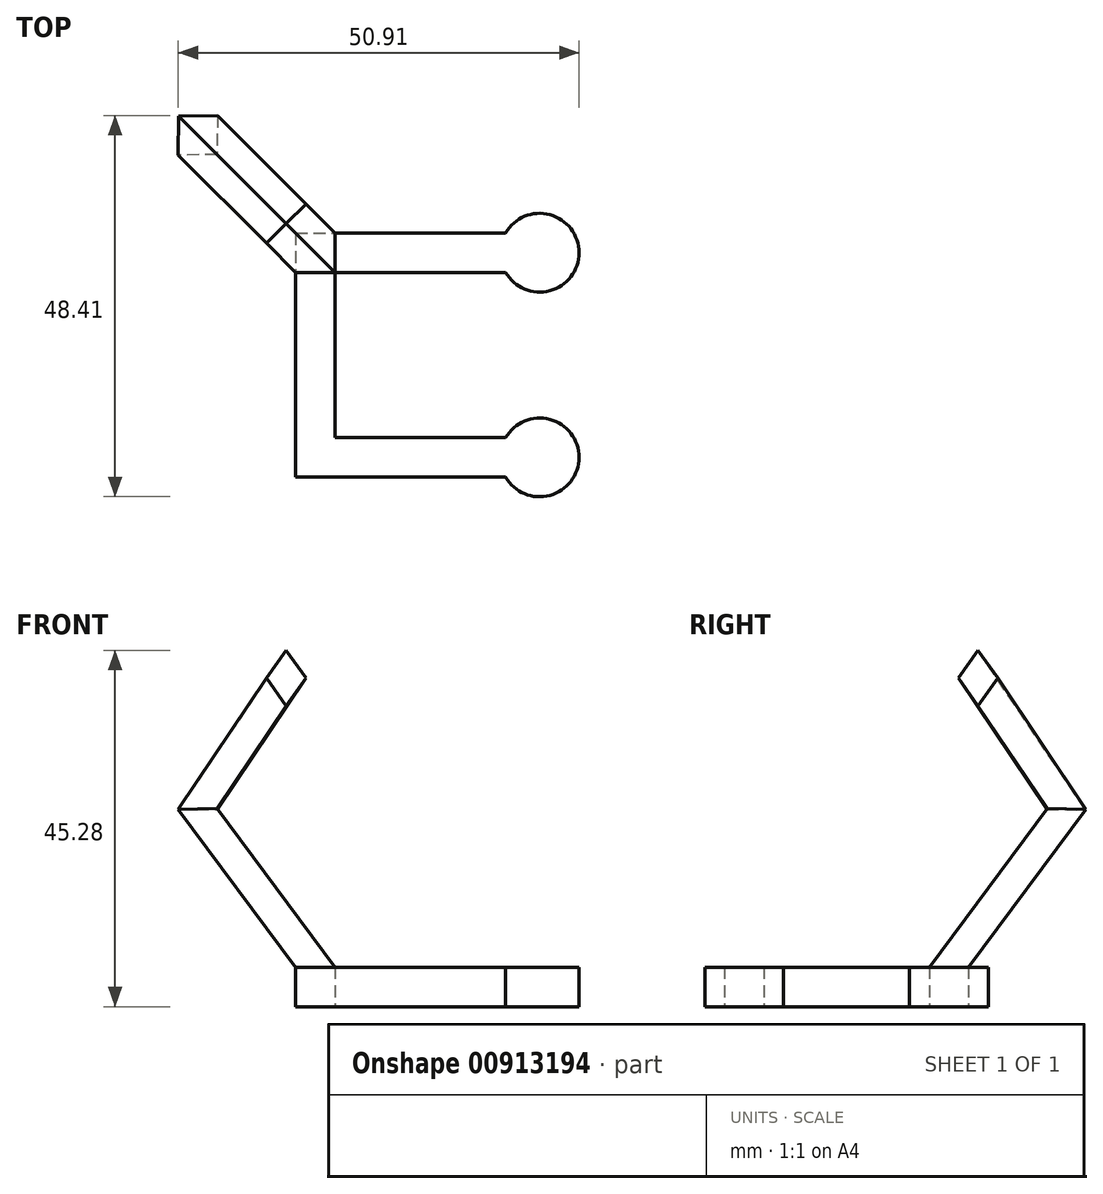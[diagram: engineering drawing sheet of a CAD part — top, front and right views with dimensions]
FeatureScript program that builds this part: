
annotation { "Feature Type Name" : "Feature", "Feature Type Description" : "" }
export const myFeature = defineFeature(function(context is Context, id is Id, definition is map)
    precondition{}
    {
        {
            assignVariable(context, id + "F0", {"name" : "HangerThickness", "anyValue" : 5});
        }
        {
            var Q0;
            Q0=qCreatedBy(makeId("Top.planeOp"),FACE);
            var sketch = newSketch(context, id + "F1", { "sketchPlane" : qUnion([Q0])});
            skLineSegment(sketch, "E0.bottom", {"start": v(10.5, 10.5) * mm, "end": v(-10.5, 10.5) * mm});
            skLineSegment(sketch, "E0.top", {"start": v(10.5, -10.5) * mm, "end": v(-10.5, -10.5) * mm});
            skLineSegment(sketch, "E0.left", {"start": v(10.5, 10.5) * mm, "end": v(10.5, -10.5) * mm});
            skLineSegment(sketch, "E0.right", {"start": v(-10.5, 10.5) * mm, "end": v(-10.5, -10.5) * mm});
            skPoint(sketch, "E0.middle", {"position": v(0, 0) * mm});
            skLineSegment(sketch, "E1.bottom", {"start": v(-15.5, 15.5) * mm, "end": v(15.5, 15.5) * mm});
            skLineSegment(sketch, "E1.top", {"start": v(-15.5, 10.5) * mm, "end": v(15.5, 10.5) * mm});
            skLineSegment(sketch, "E1.left", {"start": v(-15.5, 15.5) * mm, "end": v(-15.5, 10.5) * mm});
            skLineSegment(sketch, "E1.right", {"start": v(15.5, 15.5) * mm, "end": v(15.5, 10.5) * mm});
            skPoint(sketch, "E2", {"position": v(0, 10.5) * mm});
            skLineSegment(sketch, "E3.bottom", {"start": v(-10.5, 10.5) * mm, "end": v(-15.5, 10.5) * mm});
            skLineSegment(sketch, "E3.top", {"start": v(-10.5, -15.5) * mm, "end": v(-15.5, -15.5) * mm});
            skLineSegment(sketch, "E3.left", {"start": v(-10.5, 10.5) * mm, "end": v(-10.5, -15.5) * mm});
            skLineSegment(sketch, "E3.right", {"start": v(-15.5, 10.5) * mm, "end": v(-15.5, -15.5) * mm});
            skPoint(sketch, "E4", {"position": v(-13, -15.5) * mm});
            skPoint(sketch, "E5", {"position": v(15.5, 13) * mm});
            skCircle(sketch, "E6", {"center": v(15.5, 13) * mm, "radius": 5 * mm});
            skLineSegment(sketch, "E7.bottom", {"start": v(-10.5, -15.5) * mm, "end": v(15.5, -15.5) * mm});
            skLineSegment(sketch, "E7.top", {"start": v(-10.5, -10.5) * mm, "end": v(15.5, -10.5) * mm});
            skLineSegment(sketch, "E7.left", {"start": v(-10.5, -15.5) * mm, "end": v(-10.5, -10.5) * mm});
            skLineSegment(sketch, "E7.right", {"start": v(15.5, -15.5) * mm, "end": v(15.5, -10.5) * mm});
            skPoint(sketch, "E8", {"position": v(15.5, -13) * mm});
            skCircle(sketch, "E9", {"center": v(15.5, -13) * mm, "radius": 5 * mm});
            skSolve(sketch);
        }
        {
            var Q0;
            {var subQ0=sQuery(id+"F1.wireOp",EDGE,"E3.top");Q0=makeQuery(id+"F1.imprint","IMPRINT",FACE,{"disambiguationData":[TD([[makeQuery(id+"F1.imprint","IMPRINT",EDGE,{"derivedFrom":subQ0}),1.0]])]});}
            var Q1;
            {var subQ1=sQuery(id+"F1.wireOp",EDGE,"E0.right");Q1=makeQuery(id+"F1.imprint","IMPRINT",FACE,{"disambiguationData":[TD([[makeQuery(id+"F1.imprint","IMPRINT",EDGE,{"derivedFrom":subQ1}),-1.0]])]});}
            var Q2;
            {var subQ1=sQuery(id+"F1.wireOp",EDGE,"E0.right");Q2=makeQuery(id+"F1.imprint","IMPRINT",FACE,{"disambiguationData":[TD([[makeQuery(id+"F1.imprint","IMPRINT",EDGE,{"derivedFrom":subQ1}),-1.0]])]});}
            var Q3;
            {var subQ1=sQuery(id+"F1.wireOp",EDGE,"E0.bottom");Q3=makeQuery(id+"F1.imprint","IMPRINT",FACE,{"disambiguationData":[TD([[makeQuery(id+"F1.imprint","IMPRINT",EDGE,{"derivedFrom":subQ1}),-1.0]])]});}
            var Q4;
            {var subQ0=sQuery(id+"F1.wireOp",EDGE,"E1.right");Q4=makeQuery(id+"F1.imprint","IMPRINT",FACE,{"disambiguationData":[TD([[makeQuery(id+"F1.imprint","IMPRINT",EDGE,{"derivedFrom":subQ0}),-1.0]])]});}
            var Q5;
            {var subQ0=sQuery(id+"F1.wireOp",EDGE,"E1.right");Q5=makeQuery(id+"F1.imprint","IMPRINT",FACE,{"disambiguationData":[TD([[makeQuery(id+"F1.imprint","IMPRINT",EDGE,{"derivedFrom":subQ0}),1.0]])]});}
            var Q6;
            {var subQ1=sQuery(id+"F1.wireOp",EDGE,"E0.top");Q6=makeQuery(id+"F1.imprint","IMPRINT",FACE,{"disambiguationData":[TD([[makeQuery(id+"F1.imprint","IMPRINT",EDGE,{"derivedFrom":subQ1}),1.0]])]});}
            var Q7;
            {var subQ0=sQuery(id+"F1.wireOp",EDGE,"E7.right");Q7=makeQuery(id+"F1.imprint","IMPRINT",FACE,{"disambiguationData":[TD([[makeQuery(id+"F1.imprint","IMPRINT",EDGE,{"derivedFrom":subQ0}),1.0]])]});}
            var Q8;
            {var subQ0=sQuery(id+"F1.wireOp",EDGE,"E7.right");Q8=makeQuery(id+"F1.imprint","IMPRINT",FACE,{"disambiguationData":[TD([[makeQuery(id+"F1.imprint","IMPRINT",EDGE,{"derivedFrom":subQ0}),-1.0]])]});}
            extrude(context, id + "F2", {"entities" : qUnion([Q0, Q1, Q2, Q3, Q4, Q5, Q6, Q7, Q8]), "depth" : (getVariable(context, 'HangerThickness')) * mm, "offsetDistance" : 25 * mm});
        }
        {
            var Q0;
            Q0=makeQuery(id+"F2.opExtrude","CAP_FACE",FACE,{"disambiguationData":[OSD([sQuery(id+"F1.wireOp",EDGE,"E0.bottom"),sQuery(id+"F1.wireOp",EDGE,"E0.top"),sQuery(id+"F1.wireOp",EDGE,"E0.right"),sQuery(id+"F1.wireOp",EDGE,"E1.bottom"),sQuery(id+"F1.wireOp",EDGE,"E1.top"),sQuery(id+"F1.wireOp",EDGE,"E1.left"),sQuery(id+"F1.wireOp",EDGE,"E3.top"),sQuery(id+"F1.wireOp",EDGE,"E3.right"),sQuery(id+"F1.wireOp",EDGE,"E6"),sQuery(id+"F1.wireOp",EDGE,"E7.bottom"),sQuery(id+"F1.wireOp",EDGE,"E7.top"),sQuery(id+"F1.wireOp",EDGE,"E9")])],"isStart":false});
            var sketch = newSketch(context, id + "F3", { "sketchPlane" : qUnion([Q0])});
            skLineSegment(sketch, "E10.bottom", {"start": v(-15.5, 15.5) * mm, "end": v(-10.5, 15.5) * mm});
            skLineSegment(sketch, "E10.top", {"start": v(-15.5, 10.5) * mm, "end": v(-10.5, 10.5) * mm});
            skLineSegment(sketch, "E10.left", {"start": v(-15.5, 15.5) * mm, "end": v(-15.5, 10.5) * mm});
            skLineSegment(sketch, "E10.right", {"start": v(-10.5, 15.5) * mm, "end": v(-10.5, 10.5) * mm});
            skLineSegment(sketch, "E11", {"start": v(-15.5, 15.5) * mm, "end": v(-30.35, 30.35) * mm});
            skLineSegment(sketch, "E12", {"start": v(-30.35, 30.35) * mm, "end": v(-45.2, 45.2) * mm});
            skSolve(sketch);
        }
        {
            var Q0;
            Q0=makeQuery(id+"F2.opExtrude","CAP_FACE",FACE,{"disambiguationData":[OSD([sQuery(id+"F1.wireOp",EDGE,"E0.bottom"),sQuery(id+"F1.wireOp",EDGE,"E0.top"),sQuery(id+"F1.wireOp",EDGE,"E0.right"),sQuery(id+"F1.wireOp",EDGE,"E1.bottom"),sQuery(id+"F1.wireOp",EDGE,"E1.top"),sQuery(id+"F1.wireOp",EDGE,"E1.left"),sQuery(id+"F1.wireOp",EDGE,"E3.top"),sQuery(id+"F1.wireOp",EDGE,"E3.right"),sQuery(id+"F1.wireOp",EDGE,"E6"),sQuery(id+"F1.wireOp",EDGE,"E7.bottom"),sQuery(id+"F1.wireOp",EDGE,"E7.top"),sQuery(id+"F1.wireOp",EDGE,"E9")])],"isStart":true});
            var sketch = newSketch(context, id + "F4", { "sketchPlane" : qUnion([Q0])});
            skLineSegment(sketch, "E13.bottom", {"start": v(-15.5, -15.5) * mm, "end": v(-10.5, -15.5) * mm});
            skLineSegment(sketch, "E13.top", {"start": v(-15.5, -10.5) * mm, "end": v(-10.5, -10.5) * mm});
            skLineSegment(sketch, "E13.left", {"start": v(-15.5, -15.5) * mm, "end": v(-15.5, -10.5) * mm});
            skLineSegment(sketch, "E13.right", {"start": v(-10.5, -15.5) * mm, "end": v(-10.5, -10.5) * mm});
            skLineSegment(sketch, "E14", {"start": v(-15.5, -15.5) * mm, "end": v(-30.35, -30.35) * mm});
            skLineSegment(sketch, "E15", {"start": v(-30.35, -30.35) * mm, "end": v(-45.2, -45.2) * mm});
            skSolve(sketch);
        }
        {
            var Q0;
            Q0=sQuery(id+"F3.wireOp",EDGE,"E12");
            var Q1;
            Q1=sQuery(id+"F4.wireOp",EDGE,"E15");
            cPlane(context, id + "F5", {"entities" : qUnion([Q0, Q1]), "cplaneType" : CPlaneType.LINE_ANGLE, "offset" : 25 * mm, "angle" : 0 * degree, "width" : 150 * mm, "height" : 150 * mm});
        }
        {
            var Q0;
            Q0=qCreatedBy(id+"F5.planeOp",FACE);
            var sketch = newSketch(context, id + "F6", { "sketchPlane" : qUnion([Q0])});
            skLineSegment(sketch, "E16", {"start": v(-42.92, 0) * mm, "end": v(-42.92, 5) * mm});
            skLineSegment(sketch, "E17", {"start": v(-42.92, 0) * mm, "end": v(-42.92, 25) * mm});
            skLineSegment(sketch, "E18", {"start": v(-42.92, 25) * mm, "end": v(-21.92, 5) * mm});
            skPoint(sketch, "E19", {"position": v(-62.86, 4.07) * mm});
            skLineSegment(sketch, "E20", {"start": v(-62.86, 4.07) * mm, "end": v(-42.92, 25) * mm});
            skLineSegment(sketch, "E21", {"start": v(-42.92, 25) * mm, "end": v(-23.6, 45.28) * mm});
            skSolve(sketch);
        }
        {
            var Q0;
            Q0=makeQuery(id+"F3.imprint","IMPRINT",FACE,{"disambiguationData":[TD([[makeQuery(id+"F3.imprint","IMPRINT",EDGE,{"derivedFrom":sQuery(id+"F3.wireOp",EDGE,"E10.bottom")}),-1.0]])]});
            var Q1;
            Q1=sQuery(id+"F6.wireOp",EDGE,"E18");
            var Q2;
            Q2=sQuery(id+"F6.wireOp",EDGE,"E21");
            sweep(context, id + "F7", {"operationType" : NewBodyOperationType.ADD, "profiles" : qUnion([Q0]), "path" : qUnion([Q1, Q2])});
        }
    });
